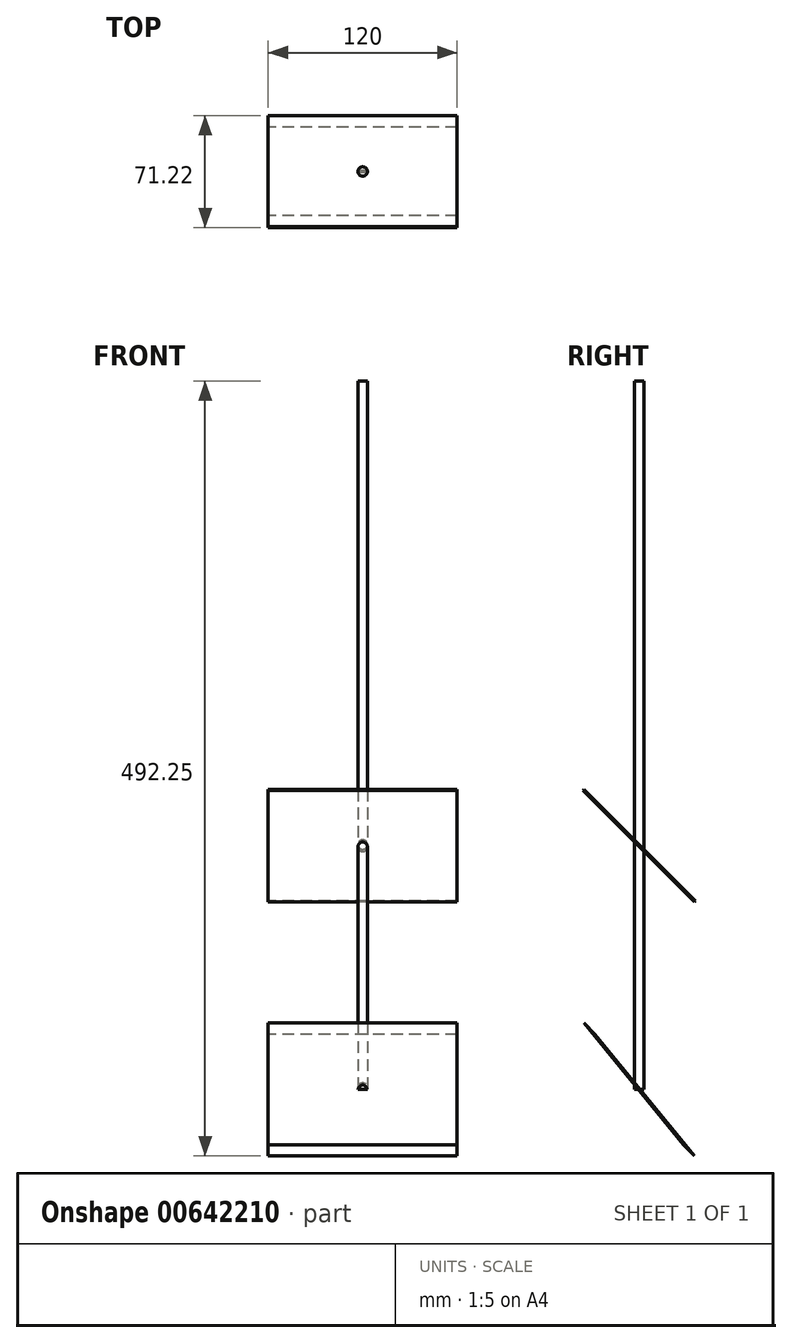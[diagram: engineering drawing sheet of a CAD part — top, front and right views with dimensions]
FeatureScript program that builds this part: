
annotation { "Feature Type Name" : "Feature", "Feature Type Description" : "" }
export const myFeature = defineFeature(function(context is Context, id is Id, definition is map)
    precondition{}
    {
        {
            var Q0;
            Q0=qCreatedBy(makeId("Top.planeOp"),FACE);
            var sketch = newSketch(context, id + "F0", { "sketchPlane" : qUnion([Q0])});
            skCircle(sketch, "E0", {"center": v(0, 0) * mm, "radius": 3 * mm});
            skSolve(sketch);
        }
        {
            var Q0;
            Q0 = qSketchRegion(id + "F0", true);
            extrude(context, id + "F1", {"entities" : qUnion([Q0]), "depth" : 450 * mm, "offsetDistance" : 25 * mm});
        }
        {
            var Q0;
            Q0=qCreatedBy(makeId("Right.planeOp"),FACE);
            var sketch = newSketch(context, id + "F2", { "sketchPlane" : qUnion([Q0])});
            skLineSegment(sketch, "E1.bottom", {"start": v(-35.18, 42.25) * mm, "end": v(28.1, -35.18) * mm});
            skLineSegment(sketch, "E1.top", {"start": v(-28.1, 35.18) * mm, "end": v(35.18, -42.25) * mm});
            skLineSegment(sketch, "E1.left", {"start": v(-35.18, 42.25) * mm, "end": v(-28.1, 35.18) * mm});
            skLineSegment(sketch, "E1.right", {"start": v(28.1, -35.18) * mm, "end": v(35.18, -42.25) * mm});
            skPoint(sketch, "E1.middle", {"position": v(0, 0) * mm});
            skLineSegment(sketch, "E2", {"start": v(0, 0) * mm, "end": v(70.71, 70.71) * mm, "construction": true});
            skLineSegment(sketch, "E3.bottom", {"start": v(35.61, 119.97) * mm, "end": v(-3.6, 159.18) * mm});
            skLineSegment(sketch, "E3.top", {"start": v(35.1, 119.11) * mm, "end": v(-35.61, 189.83) * mm});
            skLineSegment(sketch, "E3.left", {"start": v(35.61, 119.97) * mm, "end": v(35.1, 119.11) * mm});
            skLineSegment(sketch, "E3.right", {"start": v(-3.6, 159.18) * mm, "end": v(-8.76, 150.62) * mm});
            skPoint(sketch, "E3.middle", {"position": v(0, 154.9) * mm});
            skLineSegment(sketch, "E4", {"start": v(0, 154.9) * mm, "end": v(-91.16, 154.9) * mm, "construction": true});
            skPoint(sketch, "E4.endSnap0", {"position": v(-6.18, 154.9) * mm});
            skLineSegment(sketch, "E5", {"start": v(0, 154.9) * mm, "end": v(-28.06, 182.96) * mm, "construction": true});
            skLineSegment(sketch, "E6", {"start": v(-35.61, 189.83) * mm, "end": v(-34.9, 190.53) * mm});
            skLineSegment(sketch, "E7", {"start": v(-34.9, 190.53) * mm, "end": v(-3.6, 159.18) * mm});
            skSolve(sketch);
        }
        {
            var Q0;
            Q0 = qSketchRegion(id + "F2", true);
            extrude(context, id + "F3", {"entities" : qUnion([Q0]), "operationType" : NewBodyOperationType.ADD, "depth" : 60 * mm, "offsetDistance" : 25 * mm, "hasSecondDirection" : true, "secondDirectionOppositeDirection" : true, "secondDirectionDepth" : 60 * mm});
        }
    });
